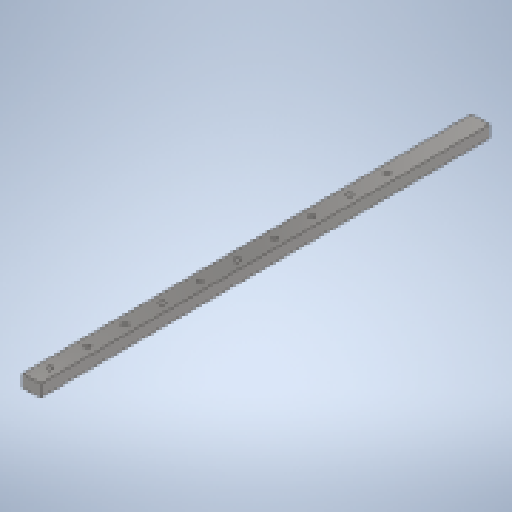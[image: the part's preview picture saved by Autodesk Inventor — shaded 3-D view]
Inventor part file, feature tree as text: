
AUTODESK INVENTOR PART (.ipt)
format: ipt  version: 2024.1 (Build 281209000, 209)  size: 261,120 bytes
history: native  units: mm
features: extrude x2, sketch x2
ambient origin geometry x8: Origin, YZ Plane, XZ Plane, XY Plane, X Axis, Y Axis, Z Axis, Center Point
bodies: Solid1 (feature_tree)
feature tree (4):
  extrude  "Extrusion1"  Depth=12.0mm
  extrude  "Extrusion2"  Depth=10.0mm
  sketch  "Sketch1"  dims[d0=300.0mm d1=12.0mm]
  sketch  "Sketch2"  dims[d2=8.0mm d3=0.0mm d4=3.5mm d5=6.0mm d6=12.5mm d7=100.0mm d9=25.0mm d10=10.0mm d12=10.0mm d14=0.0mm d15=0.0mm]
